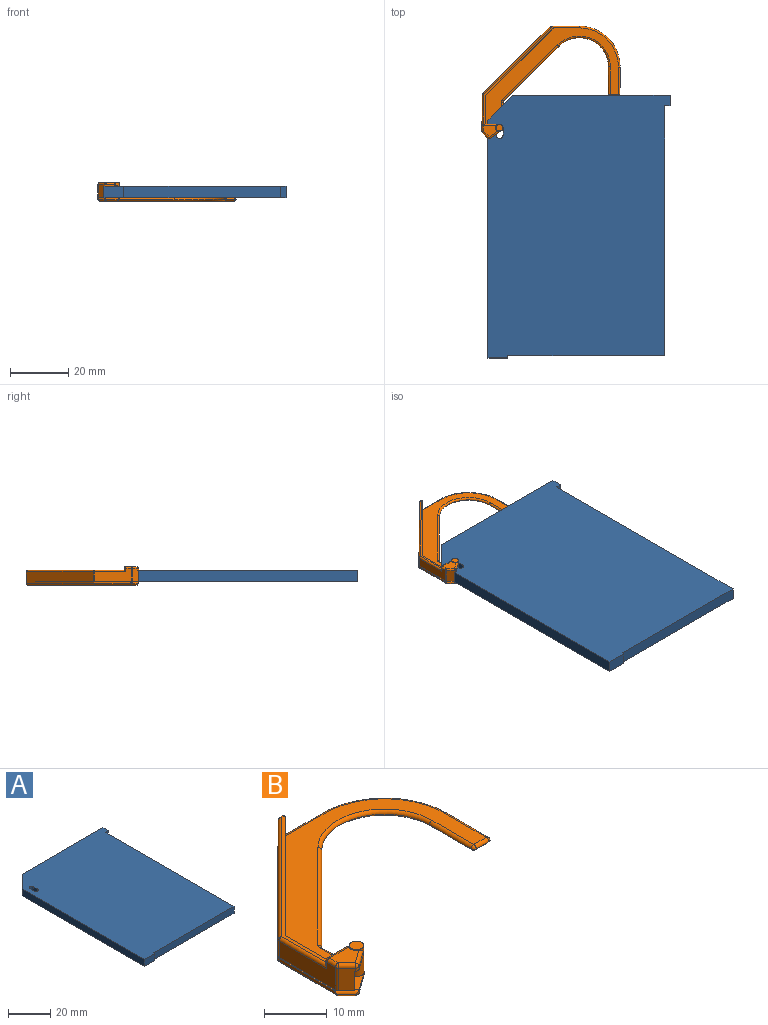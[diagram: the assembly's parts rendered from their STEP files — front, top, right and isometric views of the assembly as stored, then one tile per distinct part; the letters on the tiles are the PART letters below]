
ASSEMBLY  parts=2 mates=1
PART A: 15 faces, bbox 62.7x90.4x4 mm
  f0: plane 4x2.59mm, normal (1,0,0), area 10.4mm2, adj f1,f12,f13,f14
  f1: cylinder r=1.18mm len=4mm, axis (0,0,-1), area 14.8mm2, adj f0,f2,f13,f14
  f2: plane 4x2.59mm, normal (-1,0,0), area 10.4mm2, adj f1,f12,f13,f14
  f3: plane 4x0.8mm, normal (1,0,0), area 3.2mm2, adj f4,f11,f13,f14
  f4: plane 54x4mm, normal (0,-1,0), area 216mm2, adj f3,f5,f13,f14
  f5: plane 86x4mm, normal (1,0,0), area 344mm2, adj f4,f6,f13,f14
  f6: plane 4x1.88mm, normal (0,-1,0), area 7.5mm2, adj f5,f7,f13,f14
  f7: plane 4x3.6mm, normal (1,0,0), area 14.4mm2, adj f6,f8,f13,f14
  f8: plane 54.22x4mm, normal (0,1,0), area 216.9mm2, adj f7,f9,f13,f14
  f9: plane 8.48x8.48mm, normal (-0.71,0.71,0), area 48mm2, adj f8,f10,f13,f14
  f10: plane 81.92x4mm, normal (-1,0,0), area 327.7mm2, adj f9,f11,f13,f14
  f11: plane 6.82x4mm, normal (0,-1,0), area 27.3mm2, adj f3,f10,f13,f14
  f12: cylinder r=1.18mm len=4mm, axis (0,0,-1), area 14.8mm2, adj f0,f2,f13,f14
  f13: plane 90.4x62.7mm, normal (0,0,1), area 5415.3mm2, adj f0,f1,f2,f3,f4,f5,f6,f7
  f14: plane 90.4x62.7mm, normal (0,0,-1), area 5415.3mm2, adj f0,f1,f2,f3,f4,f5,f6,f7
PART B: 78 faces, bbox 49.6x40.9x7 mm
  f0: plane 46.86x38.16mm, normal (0,0,1), area 381.3mm2, adj f1,f4,f7,f11,f19,f22,f30,f33
  f1: plane 12.69x0.64mm, normal (-1,0,0), area 7.6mm2, adj f0,f55,f56,f57,f62
  f2: plane 33.3x23.75mm, normal (0,0,1), area 25.7mm2, adj f7,f8,f14,f38,f43,f47,f48
  f3: plane 3.8x1.7mm, normal (1,0,0), area 6.4mm2, adj f6,f10,f13,f20
  f4: plane 4.17x3.02mm, normal (0.58,-0.81,0), area 3mm2, adj f0,f52,f53,f54,f56,f70
  f5: plane 46.26x37.73mm, normal (0,0,-1), area 360.3mm2, adj f58,f61,f62,f63,f65,f66,f69,f70
  f6: plane 3.8x0.86mm, normal (0.71,0.71,0), area 4.6mm2, adj f3,f8,f13,f20
  f7: plane 22.97x22.97mm, normal (0.71,-0.71,0), area 124.4mm2, adj f0,f2,f8,f19,f20,f48
  f8: plane 12.16x3.8mm, normal (1,0,0), area 46.2mm2, adj f2,f6,f7,f13,f20
  f9: plane 12.66x4.4mm, normal (-1,0,0), area 42.8mm2, adj f20,f27,f32,f36,f38,f39
  f10: plane 4.4x1.93mm, normal (-0.71,-0.71,0), area 11.8mm2, adj f3,f13,f20,f24,f26,f27
  f11: plane 23.15x23.15mm, normal (-0.71,0.71,0), area 125.3mm2, adj f0,f19,f20,f39,f43,f48,f57,f58
  f12: plane 1.89x1.17mm, normal (1,0,0), area 0.3mm2, adj f28,f52,f53,f74
  f13: plane 5.55x5.03mm, normal (0,0,-1), area 16.3mm2, adj f3,f6,f8,f10,f14,f15,f22,f24
  f14: plane 5.47x0.6mm, normal (0,1,0), area 3mm2, adj f2,f13,f16,f18,f22,f31,f36
  f15: plane 3.88x2.79mm, normal (0.58,-0.81,0), area 2.6mm2, adj f13,f16,f18,f22,f23,f24
  f16: cylinder r=1.38mm len=2.55mm, axis (0,0,-1), area 3.2mm2, adj f14,f15,f17,f18,f23,f31
  f17: plane 4.79x3.83mm, normal (0,0,1), area 12.6mm2, adj f16,f23,f26,f31,f32
  f18: plane 2.55x2.06mm, normal (0,0,1), area 0.8mm2, adj f14,f15,f16,f22
  f19: plane 0.85x0.85mm, normal (-0.71,-0.71,0), area 0.2mm2, adj f0,f7,f11,f20
  f20: plane 35.32x20.95mm, normal (0,0,-1), area 51.5mm2, adj f3,f6,f7,f8,f9,f10,f11,f19
  f21: plane 2.35x2.35mm, normal (0,0,1), area 4.3mm2, adj f22
  f22: cylinder r=1.18mm len=5.2mm, axis (0,0,-1), area 37.5mm2, adj f0,f13,f14,f15,f18,f21,f28,f53
  f23: cylinder r=0.6mm len=3.65mm, axis (-0.81,-0.58,0), area 3.6mm2, adj f15,f16,f17,f25
  f24: cylinder r=0.6mm len=0.78mm, axis (0,0,-1), area 0.5mm2, adj f10,f13,f15,f25
  f25: sphere r=0.6mm, area 0.5mm2, adj f23,f24,f26
  f26: cylinder r=0.6mm len=2.35mm, axis (0.71,-0.71,0), area 2.6mm2, adj f10,f17,f25,f29
  f27: cylinder r=0.6mm len=4.4mm, axis (0,0,1), area 2.1mm2, adj f9,f10,f20,f29
  f28: bspline ~1.02x0.6mm, area 0.3mm2, adj f12,f22,f30
  f29: sphere r=0.6mm, area 0.3mm2, adj f26,f27,f32
  f30: cylinder r=0.6mm len=7.72mm, axis (0,1,0), area 7.3mm2, adj f0,f28,f33,f74
  f31: cylinder r=0.6mm len=4.75mm, axis (1,0,0), area 4.2mm2, adj f14,f16,f17,f34
  f32: cylinder r=0.6mm len=1.9mm, axis (0,-1,0), area 1.8mm2, adj f9,f17,f29,f34
  f33: torus R=1.2mm, axis (0,0,1), area 0.6mm2, adj f0,f30,f35,f76
  f34: sphere r=0.6mm, area 0.8mm2, adj f31,f32,f36
  f35: cylinder r=0.6mm len=19.4mm, axis (0.71,0.71,0), area 25.3mm2, adj f0,f33,f37,f77
  f36: cylinder r=0.6mm len=1.2mm, axis (0,0,1), area 0.8mm2, adj f9,f14,f34,f38
  f37: torus R=10.6mm, axis (0,0,1), area 22.7mm2, adj f0,f35,f40,f75
  f38: cylinder r=0.6mm len=10.75mm, axis (0,-1,0), area 9.9mm2, adj f2,f9,f36,f41
  f39: cylinder r=0.6mm len=3.2mm, axis (0,0,1), area 1.5mm2, adj f9,f11,f20,f41
  f40: cylinder r=0.6mm len=9.4mm, axis (0,1,0), area 8.9mm2, adj f0,f37,f42,f73
  f41: sphere r=0.6mm, area 0.3mm2, adj f38,f39,f43
  f42: sphere r=0.6mm, area 0.4mm2, adj f40,f44,f71
  f43: cylinder r=0.6mm len=23.57mm, axis (-0.71,-0.71,0), area 30.9mm2, adj f2,f11,f41,f45
  f44: cylinder r=0.6mm len=2.8mm, axis (-1,0,0), area 2.6mm2, adj f0,f42,f46,f69
  f45: sphere r=0.6mm, area 0.3mm2, adj f43,f47,f48
  f46: sphere r=0.6mm, area 0.6mm2, adj f44,f49,f67
  f47: cylinder r=0.6mm len=0.6mm, axis (-1,0,0), area 0.3mm2, adj f2,f45,f48
  f48: cylinder r=0.6mm len=4.6mm, axis (0,0,1), area 7.5mm2, adj f0,f2,f7,f11,f45,f47,f51,f59
  f49: cylinder r=0.6mm len=9.4mm, axis (0,-1,0), area 8.9mm2, adj f0,f46,f50,f65
  f50: torus R=13.4mm, axis (0,0,1), area 20.4mm2, adj f0,f49,f51,f63
  f51: cylinder r=0.6mm len=9.71mm, axis (1,0,0), area 8.9mm2, adj f0,f48,f50,f61
  f52: cylinder r=0.6mm len=0.56mm, axis (0,0,1), area 0.3mm2, adj f4,f12,f53,f72
  f53: bspline ~1x0.59mm, area 0.1mm2, adj f4,f12,f22,f52
  f54: cylinder r=0.6mm len=0.78mm, axis (0,0,-1), area 0.3mm2, adj f4,f56,f68
  f55: cylinder r=0.6mm len=0.42mm, axis (0,0,1), area 0.1mm2, adj f1,f56,f64
  f56: cylinder r=0.6mm len=3.38mm, axis (0.71,-0.71,0), area 3.3mm2, adj f0,f1,f4,f54,f55,f66
  f57: cylinder r=0.6mm len=0.6mm, axis (0,0,1), area 0.3mm2, adj f0,f1,f11,f60
  f58: plane 23.57x23.57mm, normal (-0.5,0.5,-0.71), area 27.8mm2, adj f5,f11,f59,f60
  f59: cone r=0.6mm half-angle=45deg, axis (0,0,1), area 0.3mm2, adj f48,f58,f61
  f60: cone r=0.6mm half-angle=45deg, axis (0,0,1), area 0.2mm2, adj f57,f58,f62
  f61: plane 10.17x1.06mm, normal (0,0.71,-0.71), area 8.2mm2, adj f5,f51,f59,f63
  f62: plane 12.66x0.6mm, normal (-0.71,0,-0.71), area 10.7mm2, adj f1,f5,f60,f64
  f63: cone r=14mm half-angle=45deg, axis (0,0,1), area 18.3mm2, adj f5,f50,f61,f65
  f64: cone r=0.6mm half-angle=45deg, axis (0,0,1), area 0.2mm2, adj f55,f62,f66
  f65: plane 9.4x0.6mm, normal (0.71,0,-0.71), area 8mm2, adj f5,f49,f63,f67
  f66: plane 2.35x2.35mm, normal (-0.5,-0.5,-0.71), area 2.3mm2, adj f5,f56,f64,f68
  f67: cone r=0.6mm half-angle=45deg, axis (0,0,1), area 0.4mm2, adj f46,f65,f69
  f68: cone r=0.6mm half-angle=45deg, axis (0,0,1), area 0.5mm2, adj f54,f66,f70
  f69: plane 2.8x0.6mm, normal (0,-0.71,-0.71), area 2.4mm2, adj f5,f44,f67,f71
  f70: plane 4.98x3.96mm, normal (0.41,-0.57,-0.71), area 4.3mm2, adj f4,f5,f68,f72
  f71: cone r=0.6mm half-angle=45deg, axis (0,0,1), area 0.4mm2, adj f42,f69,f73
  f72: cone r=0.6mm half-angle=45deg, axis (0,0,1), area 0.2mm2, adj f52,f70,f74
  f73: plane 9.4x0.6mm, normal (-0.71,0,-0.71), area 8mm2, adj f5,f40,f71,f75
  f74: plane 9.04x0.6mm, normal (0.71,0,-0.71), area 7.7mm2, adj f5,f12,f30,f72,f76
  f75: cone r=10.6mm half-angle=45deg, axis (0,0,-1), area 20.6mm2, adj f5,f37,f73,f77
  f76: cone r=1.2mm half-angle=45deg, axis (0,0,-1), area 0.6mm2, adj f5,f33,f74,f77
  f77: plane 19.4x19.4mm, normal (0.5,-0.5,-0.71), area 22.8mm2, adj f5,f35,f75,f76
PLACE A at identity fixed
PLACE B rot(axis=(0,0,-1),0.3deg) t=(-0.17,-0.14,0)mm
MATE revolute A.f1 <-> B.f16  axis (0,0,-1) through (-29.82,35.52,0)mm
